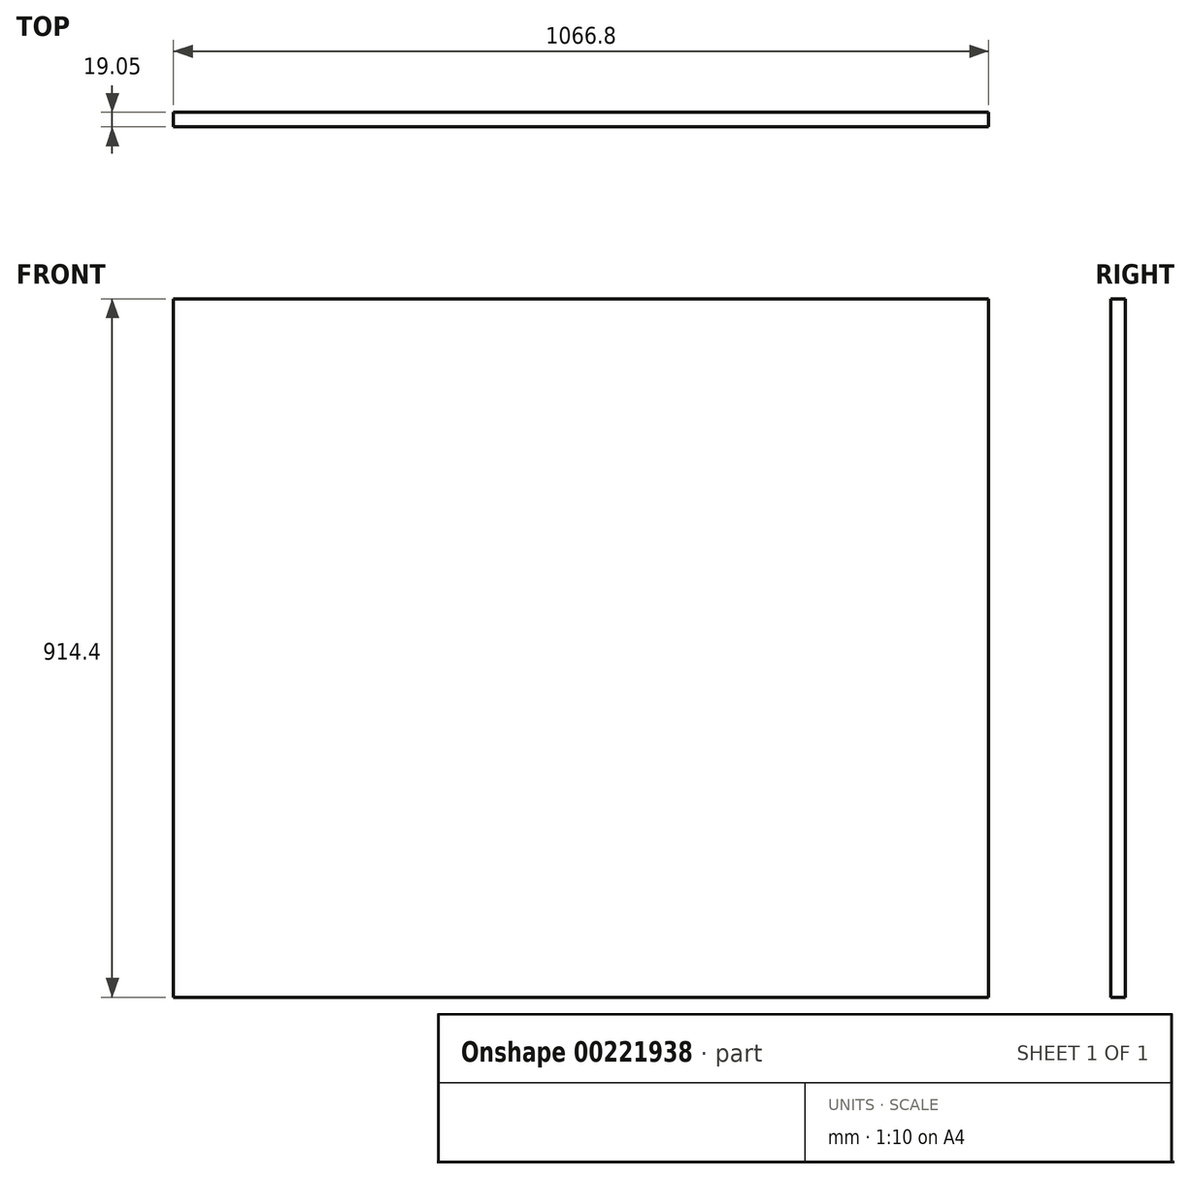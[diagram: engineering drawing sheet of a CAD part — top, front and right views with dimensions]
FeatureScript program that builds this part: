
annotation { "Feature Type Name" : "Feature", "Feature Type Description" : "" }
export const myFeature = defineFeature(function(context is Context, id is Id, definition is map)
    precondition{}
    {
        {
            var Q0;
            Q0=qCreatedBy(makeId("Front.planeOp"),FACE);
            var sketch = newSketch(context, id + "F0", { "sketchPlane" : qUnion([Q0])});
            skLineSegment(sketch, "E0.bottom", {"start": v(-484.28, 558.32) * mm, "end": v(582.52, 558.32) * mm});
            skLineSegment(sketch, "E0.top", {"start": v(-484.28, -356.08) * mm, "end": v(582.52, -356.08) * mm});
            skLineSegment(sketch, "E0.left", {"start": v(-484.28, 558.32) * mm, "end": v(-484.28, -356.08) * mm});
            skLineSegment(sketch, "E0.right", {"start": v(582.52, 558.32) * mm, "end": v(582.52, -356.08) * mm});
            skSolve(sketch);
        }
        {
            var Q0;
            Q0 = qSketchRegion(id + "F0", true);
            extrude(context, id + "F1", {"entities" : qUnion([Q0]), "depth" : 19.05 * mm});
        }
    });
